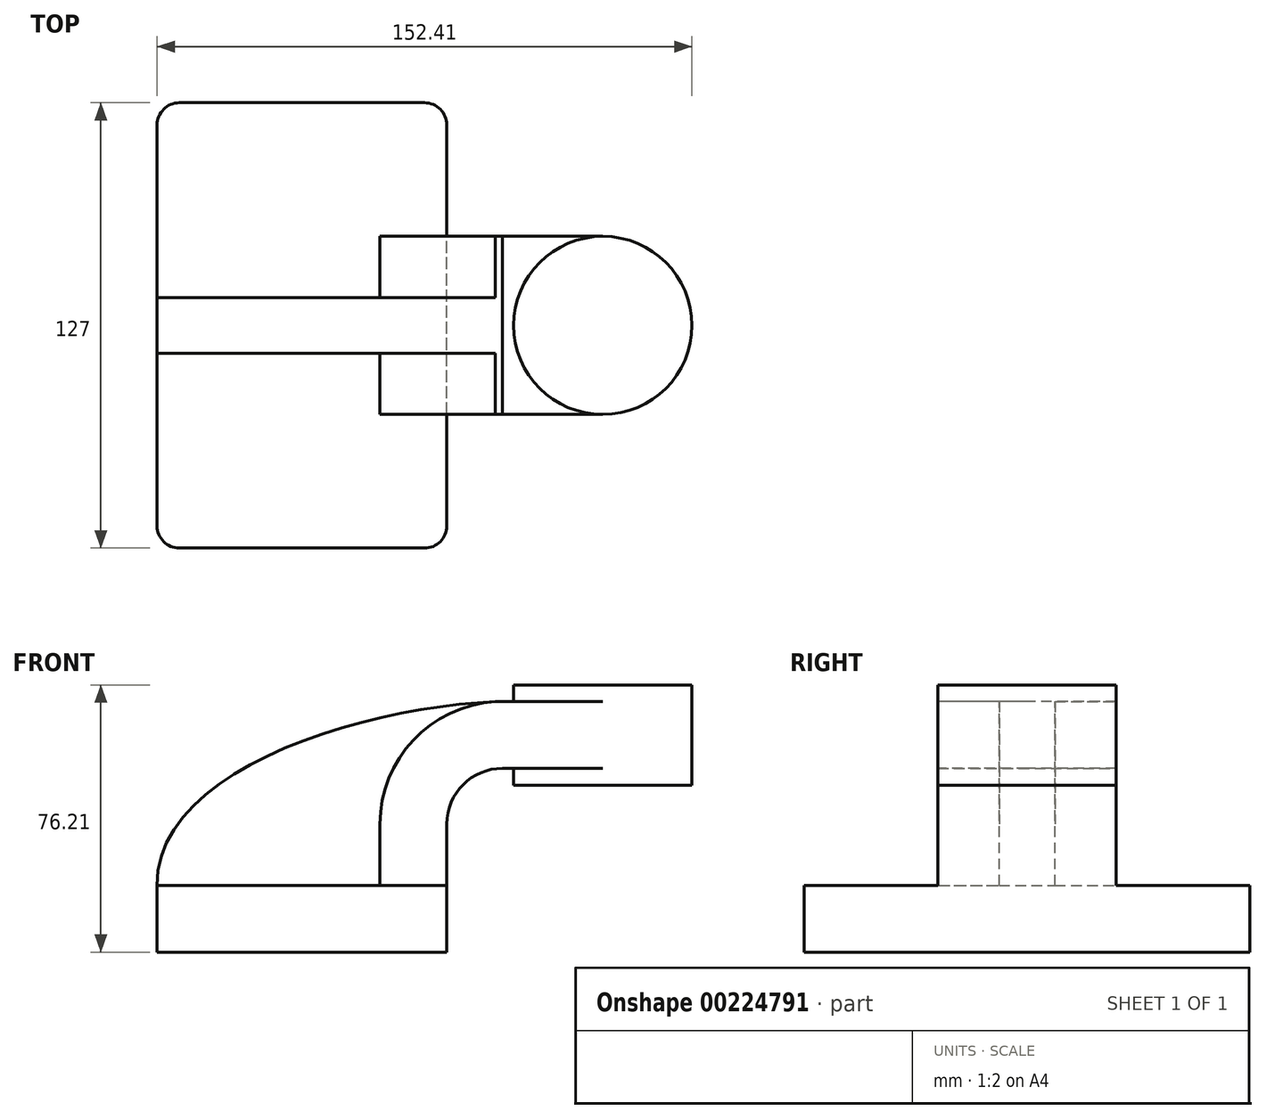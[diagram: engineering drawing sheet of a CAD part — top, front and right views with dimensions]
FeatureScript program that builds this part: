
annotation { "Feature Type Name" : "Feature", "Feature Type Description" : "" }
export const myFeature = defineFeature(function(context is Context, id is Id, definition is map)
    precondition{}
    {
        {
            var Q0;
            Q0=qCreatedBy(makeId("Front.planeOp"),FACE);
            var sketch = newSketch(context, id + "F0", { "sketchPlane" : qUnion([Q0])});
            skLineSegment(sketch, "E0.bottom", {"start": v(41.27, 9.53) * mm, "end": v(-41.28, 9.53) * mm});
            skLineSegment(sketch, "E0.top", {"start": v(41.28, -9.52) * mm, "end": v(-41.27, -9.52) * mm});
            skLineSegment(sketch, "E0.left", {"start": v(41.28, 9.53) * mm, "end": v(41.28, -9.52) * mm});
            skLineSegment(sketch, "E0.right", {"start": v(-41.28, 9.53) * mm, "end": v(-41.27, -9.52) * mm});
            skPoint(sketch, "E0.middle", {"position": v(0, 0) * mm});
            skLineSegment(sketch, "E1.bottom", {"start": v(60.33, 38.1) * mm, "end": v(111.13, 38.1) * mm});
            skLineSegment(sketch, "E1.top", {"start": v(60.33, 66.68) * mm, "end": v(111.13, 66.68) * mm});
            skLineSegment(sketch, "E1.left", {"start": v(60.33, 38.1) * mm, "end": v(60.33, 66.68) * mm});
            skLineSegment(sketch, "E1.right", {"start": v(111.13, 38.1) * mm, "end": v(111.13, 66.68) * mm});
            skPoint(sketch, "E1.middle", {"position": v(85.73, 52.39) * mm});
            skLineSegment(sketch, "E2", {"start": v(41.27, 9.53) * mm, "end": v(41.27, 27) * mm});
            skArc(sketch, "E3", {"start": v(41.27, 27) * mm, "mid": v(45.92, 38.23) * mm, "end": v(57.15, 42.88) * mm});
            skLineSegment(sketch, "E4", {"start": v(57.15, 42.88) * mm, "end": v(85.73, 42.88) * mm});
            skLineSegment(sketch, "E5.0", {"start": v(57.15, 61.93) * mm, "end": v(85.73, 61.93) * mm});
            skArc(sketch, "E5.1", {"start": v(22.23, 27) * mm, "mid": v(32.45, 51.7) * mm, "end": v(57.15, 61.93) * mm});
            skLineSegment(sketch, "E5.2", {"start": v(22.22, 9.53) * mm, "end": v(22.22, 27) * mm});
            skLineSegment(sketch, "E6", {"start": v(85.73, 38.1) * mm, "end": v(85.73, 66.68) * mm});
            skFitSpline(sketch, "E7", {"points": [v(-41.28, 9.52) * mm, v(57.15, 61.93) * mm], "startDerivative": vector(-1.29, 100.94) * mm, "endDerivative": vector(112.42, 2.51) * mm});
            skSolve(sketch);
        }
        {
            var Q0;
            Q0=makeQuery(id+"F0.imprint","IMPRINT",FACE,{"disambiguationData":[TD([[makeQuery(id+"F0.imprint","IMPRINT",EDGE,{"derivedFrom":sQuery(id+"F0.wireOp",EDGE,"E0.top")}),-1.0]])]});
            extrude(context, id + "F1", {"entities" : qUnion([Q0]), "depth" : 127 * mm, "symmetric" : true});
        }
        {
            var Q0;
            {var subQ1=sQuery(id+"F0.wireOp",EDGE,"E2");Q0=makeQuery(id+"F0.imprint","IMPRINT",FACE,{"disambiguationData":[TD([[makeQuery(id+"F0.imprint","IMPRINT",EDGE,{"derivedFrom":subQ1}),1.0]])]});}
            var Q1;
            {var subQ0=sQuery(id+"F0.wireOp",EDGE,"E4");var subQ1=sQuery(id+"F0.wireOp",EDGE,"E1.left");var subQ2=makeQuery(id+"F0.imprint","INTERSECT",VERTEX,{"derivedFrom":[subQ1,subQ0]});Q1=makeQuery(id+"F0.imprint","IMPRINT",FACE,{"disambiguationData":[TD([[makeQuery(id+"F0.imprint","IMPRINT",EDGE,{"disambiguationData":[TD([[subQ2,-1.0]])],"derivedFrom":subQ1}),-1.0]])]});}
            extrude(context, id + "F2", {"entities" : qUnion([Q0, Q1]), "operationType" : NewBodyOperationType.ADD, "depth" : 50.8 * mm, "symmetric" : true});
        }
        {
            var Q0;
            {var subQ3=sQuery(id+"F0.wireOp",EDGE,"E5.2");Q0=makeQuery(id+"F0.imprint","IMPRINT",FACE,{"disambiguationData":[TD([[makeQuery(id+"F0.imprint","IMPRINT",EDGE,{"derivedFrom":subQ3}),1.0]])]});}
            extrude(context, id + "F3", {"entities" : qUnion([Q0]), "operationType" : NewBodyOperationType.ADD, "depth" : 15.88 * mm, "symmetric" : true});
        }
        {
            var Q0;
            {var subQ0=sQuery(id+"F0.wireOp",EDGE,"E1.right");Q0=makeQuery(id+"F0.imprint","IMPRINT",FACE,{"disambiguationData":[TD([[makeQuery(id+"F0.imprint","IMPRINT",EDGE,{"derivedFrom":subQ0}),1.0]])]});}
            var Q1;
            Q1=sQuery(id+"F0.wireOp",EDGE,"E6");
            revolve(context, id + "F4", {"operationType" : NewBodyOperationType.ADD, "entities" : qUnion([Q0]), "axis" : qUnion([Q1]), "revolveType" : RevolveType.FULL});
        }
        {
            var Q0;
            Q0=makeQuery(id+"F1.opExtrude","CAP_EDGE",EDGE,{"disambiguationData":[OSD([sQuery(id+"F0.wireOp",EDGE,"E0.right")])],"isStart":false});
            var Q1;
            Q1=makeQuery(id+"F1.opExtrude","CAP_EDGE",EDGE,{"disambiguationData":[OSD([sQuery(id+"F0.wireOp",EDGE,"E0.left")])],"isStart":false});
            var Q2;
            Q2=makeQuery(id+"F1.opExtrude","CAP_EDGE",EDGE,{"disambiguationData":[OSD([sQuery(id+"F0.wireOp",EDGE,"E0.left")])],"isStart":true});
            var Q3;
            Q3=makeQuery(id+"F1.opExtrude","CAP_EDGE",EDGE,{"disambiguationData":[OSD([sQuery(id+"F0.wireOp",EDGE,"E0.right")])],"isStart":true});
            fillet(context, id + "F5", {"entities" : qUnion([Q0, Q1, Q2, Q3]), "radius" : 6.35 * mm, "tangentPropagation" : true, "allowEdgeOverflow" : false});
        }
    });
